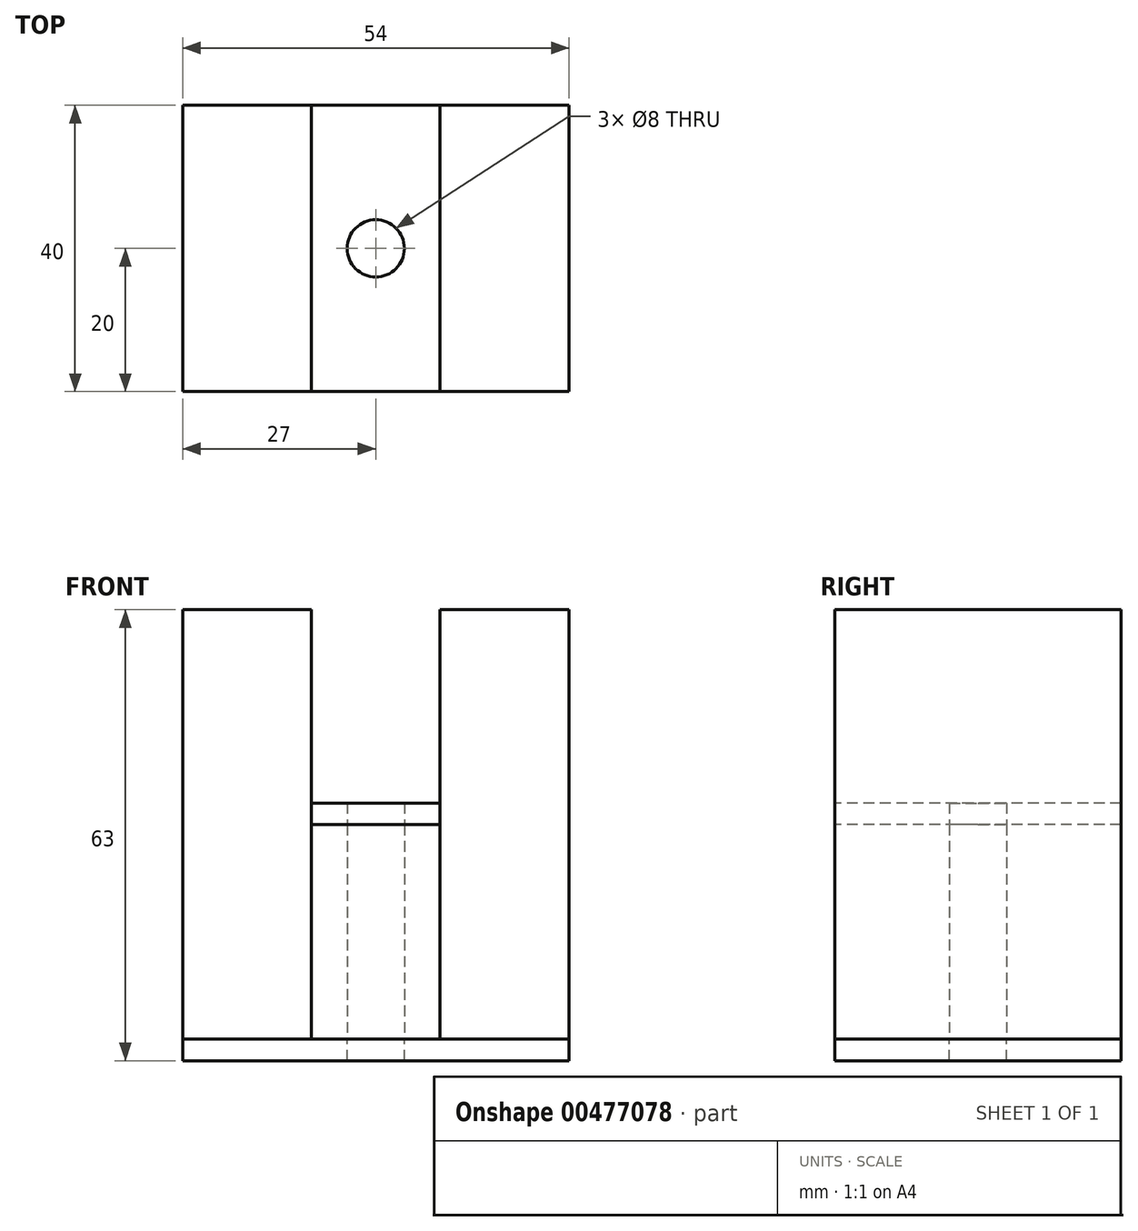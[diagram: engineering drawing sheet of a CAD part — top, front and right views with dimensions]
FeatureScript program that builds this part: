
annotation { "Feature Type Name" : "Feature", "Feature Type Description" : "" }
export const myFeature = defineFeature(function(context is Context, id is Id, definition is map)
    precondition{}
    {
        {
            var Q0;
            Q0=qCreatedBy(makeId("Top.planeOp"),FACE);
            var sketch = newSketch(context, id + "F0", { "sketchPlane" : qUnion([Q0])});
            skLineSegment(sketch, "E0.bottom", {"start": v(9, 20) * mm, "end": v(-9, 20) * mm});
            skLineSegment(sketch, "E0.top", {"start": v(9, -20) * mm, "end": v(-9, -20) * mm});
            skLineSegment(sketch, "E0.left", {"start": v(9, 20) * mm, "end": v(9, -20) * mm});
            skLineSegment(sketch, "E0.right", {"start": v(-9, 20) * mm, "end": v(-9, -20) * mm});
            skPoint(sketch, "E0.middle", {"position": v(0, 0) * mm});
            skLineSegment(sketch, "E1.bottom", {"start": v(-9, 20) * mm, "end": v(-27, 20) * mm});
            skLineSegment(sketch, "E1.top", {"start": v(-9, -20) * mm, "end": v(-27, -20) * mm});
            skLineSegment(sketch, "E1.right", {"start": v(-27, 20) * mm, "end": v(-27, -20) * mm});
            skLineSegment(sketch, "E2.bottom", {"start": v(9, 20) * mm, "end": v(27, 20) * mm});
            skLineSegment(sketch, "E2.top", {"start": v(9, -20) * mm, "end": v(27, -20) * mm});
            skLineSegment(sketch, "E2.right", {"start": v(27, 20) * mm, "end": v(27, -20) * mm});
            skSolve(sketch);
        }
        {
            var Q0;
            {var subQ3=sQuery(id+"F0.wireOp",EDGE,"E1.bottom");Q0=makeQuery(id+"F0.imprint","IMPRINT",FACE,{"disambiguationData":[TD([[makeQuery(id+"F0.imprint","IMPRINT",EDGE,{"derivedFrom":subQ3}),1.0]])]});}
            var Q1;
            {var subQ3=sQuery(id+"F0.wireOp",EDGE,"E2.bottom");Q1=makeQuery(id+"F0.imprint","IMPRINT",FACE,{"disambiguationData":[TD([[makeQuery(id+"F0.imprint","IMPRINT",EDGE,{"derivedFrom":subQ3}),-1.0]])]});}
            extrude(context, id + "F1", {"entities" : qUnion([Q0, Q1]), "depth" : 60 * mm});
        }
        {
            var Q0;
            {var subQ0=sQuery(id+"F0.wireOp",EDGE,"E0.bottom");Q0=makeQuery(id+"F0.imprint","IMPRINT",FACE,{"disambiguationData":[TD([[makeQuery(id+"F0.imprint","IMPRINT",EDGE,{"derivedFrom":subQ0}),1.0]])]});}
            extrude(context, id + "F2", {"entities" : qUnion([Q0]), "depth" : 30 * mm});
        }
        {
            var Q0;
            Q0=sQuery(id+"F0.wireOp",VERTEX,"E0.middle");
            var Q1;
            Q1=makeQuery(id+"F2.opExtrude","SWEPT_BODY",BODY,{"disambiguationData":[OSD([sQuery(id+"F0.wireOp",EDGE,"E0.bottom"),sQuery(id+"F0.wireOp",EDGE,"E0.top"),sQuery(id+"F0.wireOp",EDGE,"E0.right"),sQuery(id+"F0.wireOp",EDGE,"E0.left")])]});
            hole(context, id + "F3", {"style" : HoleStyle.SIMPLE, "endStyle" : HoleEndStyle.THROUGH, "oppositeDirection" : true, "holeDiameter" : 8 * mm, "isTappedThrough" : true, "tappedDepth" : 12 * mm, "tapClearance" : 3, "locations" : qUnion([Q0]), "scope" : qUnion([Q1])});
        }
        {
            var Q0;
            Q0=makeQuery(id+"F0.imprint","IMPRINT",FACE,{"disambiguationData":[TD([[makeQuery(id+"F0.imprint","IMPRINT",EDGE,{"derivedFrom":sQuery(id+"F0.wireOp",EDGE,"E1.bottom")}),1.0]])]});
            var Q1;
            Q1=makeQuery(id+"F0.imprint","IMPRINT",FACE,{"disambiguationData":[TD([[makeQuery(id+"F0.imprint","IMPRINT",EDGE,{"derivedFrom":sQuery(id+"F0.wireOp",EDGE,"E0.bottom")}),1.0]])]});
            var Q2;
            Q2=makeQuery(id+"F0.imprint","IMPRINT",FACE,{"disambiguationData":[TD([[makeQuery(id+"F0.imprint","IMPRINT",EDGE,{"derivedFrom":sQuery(id+"F0.wireOp",EDGE,"E2.bottom")}),-1.0]])]});
            extrude(context, id + "F4", {"entities" : qUnion([Q0, Q1, Q2]), "oppositeDirection" : true, "depth" : 3 * mm});
        }
        {
            var Q0;
            Q0=sQuery(id+"F0.wireOp",VERTEX,"E0.middle");
            var Q1;
            Q1=makeQuery(id+"F4.opExtrude","SWEPT_BODY",BODY,{"disambiguationData":[OSD([sQuery(id+"F0.wireOp",EDGE,"E0.bottom"),sQuery(id+"F0.wireOp",EDGE,"E0.top"),sQuery(id+"F0.wireOp",EDGE,"E1.bottom"),sQuery(id+"F0.wireOp",EDGE,"E1.top"),sQuery(id+"F0.wireOp",EDGE,"E1.right"),sQuery(id+"F0.wireOp",EDGE,"E2.bottom"),sQuery(id+"F0.wireOp",EDGE,"E2.top"),sQuery(id+"F0.wireOp",EDGE,"E2.right")])]});
            hole(context, id + "F5", {"style" : HoleStyle.SIMPLE, "endStyle" : HoleEndStyle.THROUGH, "holeDiameter" : 8 * mm, "isTappedThrough" : true, "tappedDepth" : 12 * mm, "tapClearance" : 3, "locations" : qUnion([Q0]), "scope" : qUnion([Q1])});
        }
        {
            var Q0;
            Q0=makeQuery(id+"F2.opExtrude","CAP_FACE",FACE,{"disambiguationData":[OSD([sQuery(id+"F0.wireOp",EDGE,"E0.bottom"),sQuery(id+"F0.wireOp",EDGE,"E0.top"),sQuery(id+"F0.wireOp",EDGE,"E0.right"),sQuery(id+"F0.wireOp",EDGE,"E0.left")])],"isStart":false});
            var sketch = newSketch(context, id + "F6", { "sketchPlane" : qUnion([Q0])});
            skLineSegment(sketch, "E3.0.0", {"start": v(-9, -20) * mm, "end": v(9, -20) * mm});
            skLineSegment(sketch, "E3.0.1", {"start": v(9, -20) * mm, "end": v(9, 20) * mm});
            skLineSegment(sketch, "E3.0.2", {"start": v(9, 20) * mm, "end": v(-9, 20) * mm});
            skLineSegment(sketch, "E3.0.3", {"start": v(-9, 20) * mm, "end": v(-9, -20) * mm});
            skSolve(sketch);
        }
        {
            var Q0;
            Q0=makeQuery(id+"F6.imprint","IMPRINT",FACE,{"disambiguationData":[TD([[makeQuery(id+"F6.imprint","IMPRINT",EDGE,{"derivedFrom":sQuery(id+"F6.wireOp",EDGE,"E3.0.0")}),-1.0]])]});
            extrude(context, id + "F7", {"entities" : qUnion([Q0]), "depth" : 3 * mm});
        }
    });
